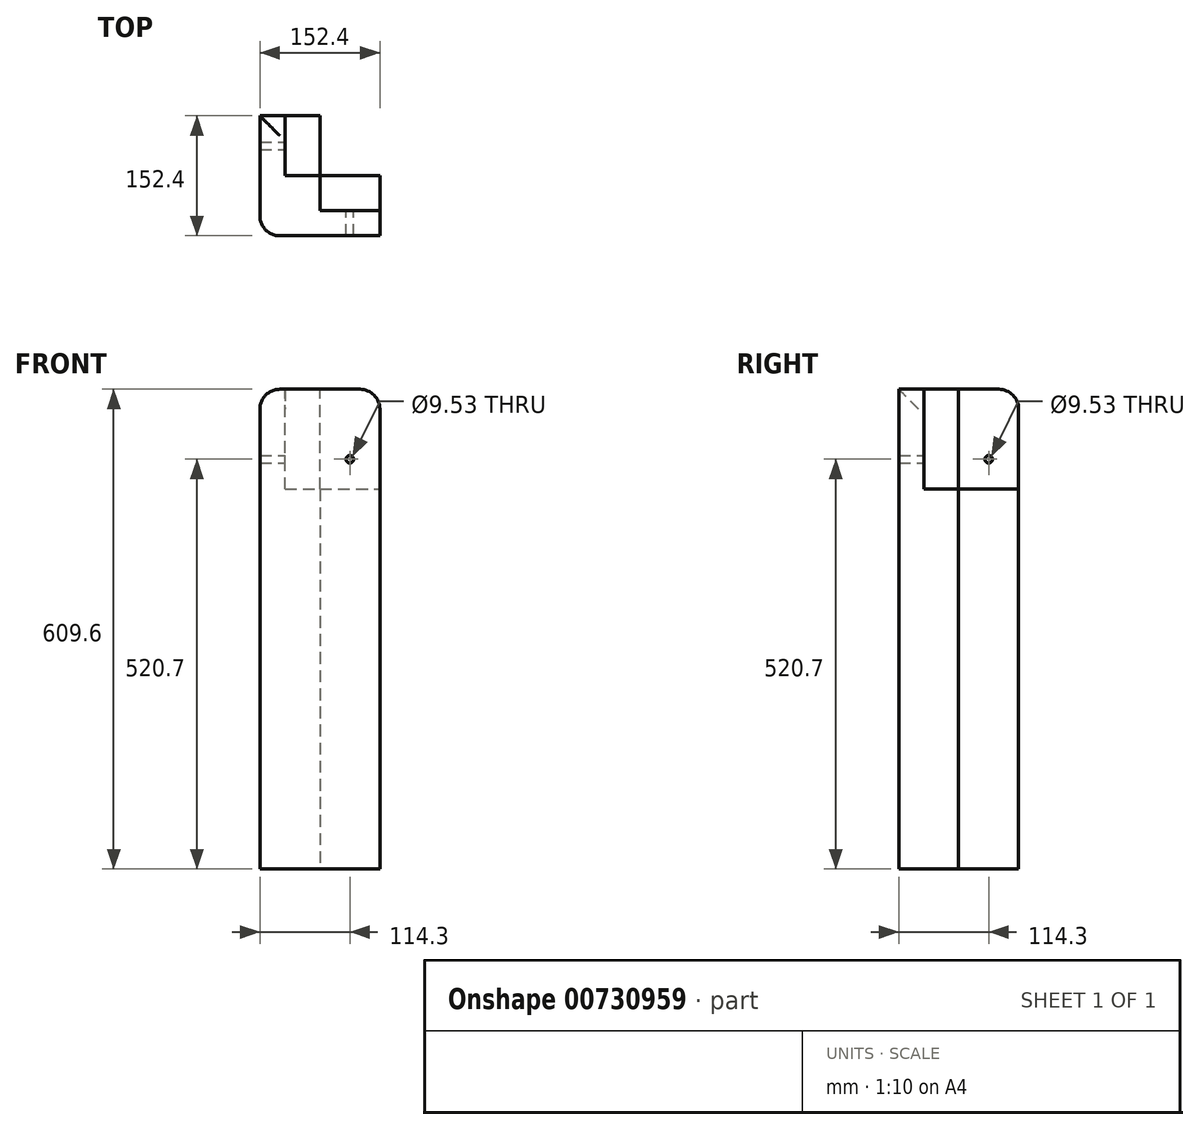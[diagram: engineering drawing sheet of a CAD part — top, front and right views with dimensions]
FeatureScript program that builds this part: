
annotation { "Feature Type Name" : "Feature", "Feature Type Description" : "" }
export const myFeature = defineFeature(function(context is Context, id is Id, definition is map)
    precondition{}
    {
        {
            var Q0;
            Q0=qCreatedBy(makeId("Top.planeOp"),FACE);
            var sketch = newSketch(context, id + "F0", { "sketchPlane" : qUnion([Q0])});
            skLineSegment(sketch, "E0.bottom", {"start": v(0, 0) * mm, "end": v(76.2, 0) * mm});
            skLineSegment(sketch, "E0.top", {"start": v(0, 76.2) * mm, "end": v(76.2, 76.2) * mm});
            skLineSegment(sketch, "E0.left", {"start": v(0, 0) * mm, "end": v(0, 76.2) * mm});
            skLineSegment(sketch, "E0.right", {"start": v(76.2, 0) * mm, "end": v(76.2, 76.2) * mm});
            skSolve(sketch);
        }
        {
            var Q0;
            Q0 = qSketchRegion(id + "F0", true);
            extrude(context, id + "F1", {"entities" : qUnion([Q0]), "depth" : 558.8 * mm, "offsetDistance" : 25.4 * mm});
        }
        {
            var Q0;
            Q0=makeQuery(id+"F1.opExtrude","SWEPT_BODY",BODY,{"disambiguationData":[OSD([sQuery(id+"F0.wireOp",EDGE,"E0.bottom"),sQuery(id+"F0.wireOp",EDGE,"E0.top"),sQuery(id+"F0.wireOp",EDGE,"E0.left"),sQuery(id+"F0.wireOp",EDGE,"E0.right")])]});
            var Q1;
            Q1=makeQuery(id+"F1.opExtrude","CAP_EDGE",EDGE,{"disambiguationData":[OSD([sQuery(id+"F0.wireOp",EDGE,"E0.bottom")])],"isStart":true});
            transform(context, id + "F2", {"entities" : qUnion([Q0]), "transformType" : TransformType.TRANSLATION_ENTITY, "oppositeDirectionEntity" : false, "transformLine" : qUnion([Q1]), "makeCopy" : true});
        }
        {
            var Q0;
            Q0=makeQuery(id+"F1.opExtrude","SWEPT_BODY",BODY,{"disambiguationData":[OSD([sQuery(id+"F0.wireOp",EDGE,"E0.bottom"),sQuery(id+"F0.wireOp",EDGE,"E0.top"),sQuery(id+"F0.wireOp",EDGE,"E0.left"),sQuery(id+"F0.wireOp",EDGE,"E0.right")])]});
            var Q1;
            Q1=makeQuery(id+"F1.opExtrude","CAP_EDGE",EDGE,{"disambiguationData":[OSD([sQuery(id+"F0.wireOp",EDGE,"E0.left")])],"isStart":true});
            transform(context, id + "F3", {"entities" : qUnion([Q0]), "transformType" : TransformType.TRANSLATION_ENTITY, "oppositeDirectionEntity" : false, "transformLine" : qUnion([Q1]), "makeCopy" : true});
        }
        {
            var Q0;
            Q0=makeQuery(id+"F3.opPattern","COPY",FACE,{"derivedFrom":makeQuery(id+"F1.opExtrude","CAP_FACE",FACE,{"disambiguationData":[OSD([sQuery(id+"F0.wireOp",EDGE,"E0.bottom"),sQuery(id+"F0.wireOp",EDGE,"E0.top"),sQuery(id+"F0.wireOp",EDGE,"E0.left"),sQuery(id+"F0.wireOp",EDGE,"E0.right")])],"isStart":false}),"instanceName":"1"});
            extrude(context, id + "F4", {"entities" : qUnion([Q0]), "operationType" : NewBodyOperationType.ADD, "depth" : 50.8 * mm, "offsetDistance" : 25.4 * mm});
        }
        {
            var Q0;
            Q0=makeQuery(id+"F2.opPattern","COPY",FACE,{"derivedFrom":makeQuery(id+"F1.opExtrude","CAP_FACE",FACE,{"disambiguationData":[OSD([sQuery(id+"F0.wireOp",EDGE,"E0.bottom"),sQuery(id+"F0.wireOp",EDGE,"E0.top"),sQuery(id+"F0.wireOp",EDGE,"E0.left"),sQuery(id+"F0.wireOp",EDGE,"E0.right")])],"isStart":false}),"instanceName":"1"});
            extrude(context, id + "F5", {"entities" : qUnion([Q0]), "operationType" : NewBodyOperationType.ADD, "depth" : 50.8 * mm, "offsetDistance" : 25.4 * mm});
        }
        {
            var Q0;
            Q0=makeQuery(id+"F4.opExtrude","CAP_FACE",FACE,{"disambiguationData":[OSD([sQuery(id+"F0.wireOp",EDGE,"E0.bottom"),sQuery(id+"F0.wireOp",EDGE,"E0.top"),sQuery(id+"F0.wireOp",EDGE,"E0.left"),sQuery(id+"F0.wireOp",EDGE,"E0.right")])],"isStart":false});
            var sketch = newSketch(context, id + "F6", { "sketchPlane" : qUnion([Q0])});
            skLineSegment(sketch, "E1.bottom", {"start": v(76.2, 152.4) * mm, "end": v(31.75, 152.4) * mm});
            skLineSegment(sketch, "E1.top", {"start": v(76.2, 76.2) * mm, "end": v(31.75, 76.2) * mm});
            skLineSegment(sketch, "E1.left", {"start": v(76.2, 152.4) * mm, "end": v(76.2, 76.2) * mm});
            skLineSegment(sketch, "E1.right", {"start": v(31.75, 152.4) * mm, "end": v(31.75, 76.2) * mm});
            skSolve(sketch);
        }
        {
            var Q0;
            Q0 = qSketchRegion(id + "F6", true);
            extrude(context, id + "F7", {"entities" : qUnion([Q0]), "operationType" : NewBodyOperationType.REMOVE, "oppositeDirection" : true, "depth" : 127 * mm, "offsetDistance" : 25.4 * mm});
        }
        {
            var Q0;
            Q0=makeQuery(id+"F5.opExtrude","CAP_FACE",FACE,{"disambiguationData":[OSD([sQuery(id+"F0.wireOp",EDGE,"E0.bottom"),sQuery(id+"F0.wireOp",EDGE,"E0.top"),sQuery(id+"F0.wireOp",EDGE,"E0.left"),sQuery(id+"F0.wireOp",EDGE,"E0.right")])],"isStart":false});
            var sketch = newSketch(context, id + "F8", { "sketchPlane" : qUnion([Q0])});
            skLineSegment(sketch, "E2.bottom", {"start": v(152.4, 76.2) * mm, "end": v(76.2, 76.2) * mm});
            skLineSegment(sketch, "E2.top", {"start": v(152.4, 31.75) * mm, "end": v(76.2, 31.75) * mm});
            skLineSegment(sketch, "E2.left", {"start": v(152.4, 76.2) * mm, "end": v(152.4, 31.75) * mm});
            skLineSegment(sketch, "E2.right", {"start": v(76.2, 76.2) * mm, "end": v(76.2, 31.75) * mm});
            skSolve(sketch);
        }
        {
            var Q0;
            Q0 = qSketchRegion(id + "F8", true);
            extrude(context, id + "F9", {"entities" : qUnion([Q0]), "operationType" : NewBodyOperationType.REMOVE, "oppositeDirection" : true, "depth" : 127 * mm, "offsetDistance" : 25.4 * mm});
        }
        {
            var Q0;
            Q0=makeQuery(id+"F1.opExtrude","SWEPT_EDGE",EDGE,{"disambiguationData":[OSD([sQuery(id+"F0.wireOp",EDGE,"E0.bottom"),sQuery(id+"F0.wireOp",EDGE,"E0.left")])]});
            var Q1;
            Q1=makeQuery(id+"F5.opExtrude","CAP_EDGE",EDGE,{"disambiguationData":[OSD([sQuery(id+"F0.wireOp",EDGE,"E0.left")])],"isStart":false});
            var Q2;
            Q2=makeQuery(id+"F5.opExtrude","CAP_EDGE",EDGE,{"disambiguationData":[OSD([sQuery(id+"F0.wireOp",EDGE,"E0.right")])],"isStart":false});
            var Q3;
            Q3=makeQuery(id+"F4.opExtrude","CAP_EDGE",EDGE,{"disambiguationData":[OSD([sQuery(id+"F0.wireOp",EDGE,"E0.bottom")])],"isStart":false});
            var Q4;
            Q4=makeQuery(id+"F4.opExtrude","CAP_EDGE",EDGE,{"disambiguationData":[OSD([sQuery(id+"F0.wireOp",EDGE,"E0.top")])],"isStart":false});
            fillet(context, id + "F10", {"entities" : qUnion([Q0, Q1, Q2, Q3, Q4]), "radius" : 25.4 * mm, "tangentPropagation" : true, "allowEdgeOverflow" : false});
        }
        {
            var Q0;
            Q0=makeQuery(id+"F7.boolean.opBoolean","COPY",FACE,{"derivedFrom":makeQuery(id+"F7.opExtrude","SWEPT_FACE",FACE,{"disambiguationData":[OSD([sQuery(id+"F6.wireOp",EDGE,"E1.right")])]})});
            var sketch = newSketch(context, id + "F11", { "sketchPlane" : qUnion([Q0])});
            skCircle(sketch, "E3", {"center": v(114.3, 520.7) * mm, "radius": 4.76 * mm});
            skSolve(sketch);
        }
        {
            var Q0;
            Q0 = qSketchRegion(id + "F11", true);
            extrude(context, id + "F12", {"entities" : qUnion([Q0]), "operationType" : NewBodyOperationType.REMOVE, "endBound" : BoundingType.THROUGH_ALL, "oppositeDirection" : true, "depth" : 25.4 * mm, "offsetDistance" : 25.4 * mm});
        }
        {
            var Q0;
            Q0=makeQuery(id+"F9.boolean.opBoolean","COPY",FACE,{"derivedFrom":makeQuery(id+"F9.opExtrude","SWEPT_FACE",FACE,{"disambiguationData":[OSD([sQuery(id+"F8.wireOp",EDGE,"E2.top")])]})});
            var sketch = newSketch(context, id + "F13", { "sketchPlane" : qUnion([Q0])});
            skCircle(sketch, "E4", {"center": v(-114.3, 520.7) * mm, "radius": 4.76 * mm});
            skSolve(sketch);
        }
        {
            var Q0;
            Q0 = qSketchRegion(id + "F13", true);
            extrude(context, id + "F14", {"entities" : qUnion([Q0]), "operationType" : NewBodyOperationType.REMOVE, "endBound" : BoundingType.THROUGH_ALL, "oppositeDirection" : true, "depth" : 25.4 * mm, "offsetDistance" : 25.4 * mm});
        }
    });
